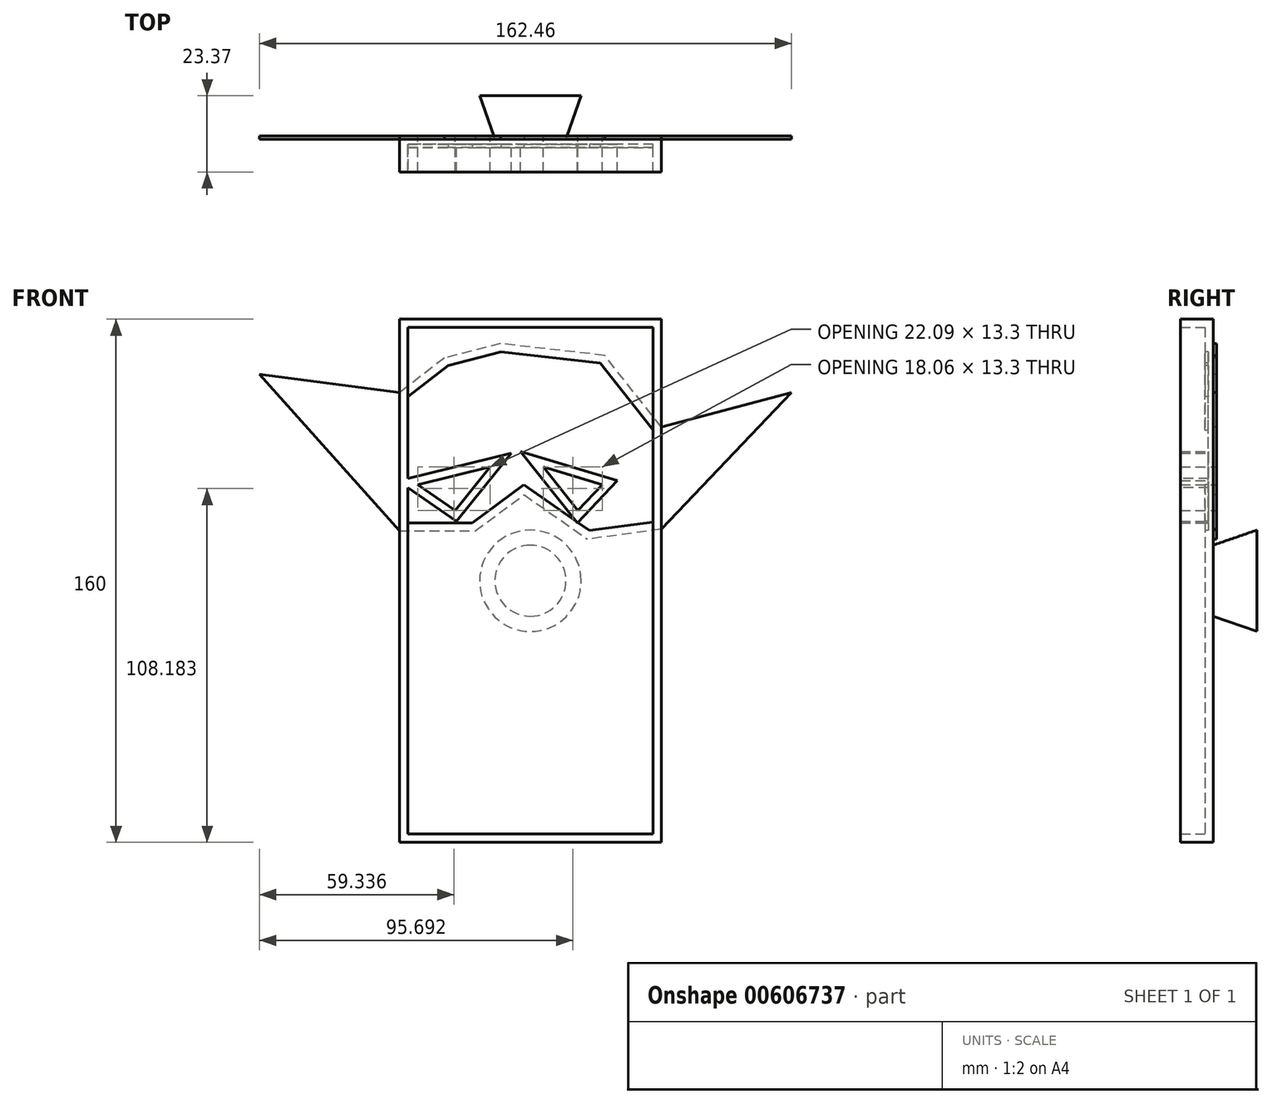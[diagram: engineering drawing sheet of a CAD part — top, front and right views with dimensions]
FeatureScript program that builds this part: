
annotation { "Feature Type Name" : "Feature", "Feature Type Description" : "" }
export const myFeature = defineFeature(function(context is Context, id is Id, definition is map)
    precondition{}
    {
        {
            var Q0;
            Q0=qCreatedBy(makeId("Front.planeOp"),FACE);
            var sketch = newSketch(context, id + "F0", { "sketchPlane" : qUnion([Q0])});
            skLineSegment(sketch, "E0.bottom", {"start": v(-40, 80) * mm, "end": v(40, 80) * mm});
            skLineSegment(sketch, "E0.top", {"start": v(-40, -80) * mm, "end": v(40, -80) * mm});
            skLineSegment(sketch, "E0.left", {"start": v(-40, 80) * mm, "end": v(-40, -80) * mm});
            skLineSegment(sketch, "E0.right", {"start": v(40, 80) * mm, "end": v(40, -80) * mm});
            skPoint(sketch, "E0.middle", {"position": v(0, 0) * mm});
            skSolve(sketch);
        }
        {
            var Q0;
            Q0=makeQuery(id+"F0.imprint","IMPRINT",FACE,{"disambiguationData":[TD([[makeQuery(id+"F0.imprint","IMPRINT",EDGE,{"derivedFrom":sQuery(id+"F0.wireOp",EDGE,"E0.bottom")}),-1.0]])]});
            extrude(context, id + "F1", {"entities" : qUnion([Q0]), "depth" : 10 * mm, "offsetDistance" : 25 * mm});
        }
        {
            var Q0;
            Q0=makeQuery(id+"F1.opExtrude","CAP_FACE",FACE,{"disambiguationData":[OSD([sQuery(id+"F0.wireOp",EDGE,"E0.bottom"),sQuery(id+"F0.wireOp",EDGE,"E0.top"),sQuery(id+"F0.wireOp",EDGE,"E0.left"),sQuery(id+"F0.wireOp",EDGE,"E0.right")])],"isStart":true});
            var sketch = newSketch(context, id + "F2", { "sketchPlane" : qUnion([Q0])});
            skLineSegment(sketch, "E1", {"start": v(-40, 15.78) * mm, "end": v(-79.71, 57.57) * mm});
            skLineSegment(sketch, "E2", {"start": v(-79.71, 57.57) * mm, "end": v(-40, 47.05) * mm});
            skLineSegment(sketch, "E3", {"start": v(-40, 47.05) * mm, "end": v(-22.7, 68.92) * mm});
            skLineSegment(sketch, "E4", {"start": v(-22.7, 68.92) * mm, "end": v(9.13, 72.51) * mm});
            skLineSegment(sketch, "E5", {"start": v(9.13, 72.51) * mm, "end": v(26.3, 68.09) * mm});
            skLineSegment(sketch, "E6", {"start": v(26.3, 68.09) * mm, "end": v(40, 57.57) * mm});
            skLineSegment(sketch, "E7", {"start": v(40, 57.57) * mm, "end": v(82.75, 63.1) * mm});
            skLineSegment(sketch, "E8", {"start": v(82.75, 63.1) * mm, "end": v(40, 15.22) * mm});
            skLineSegment(sketch, "E9", {"start": v(40, 15.22) * mm, "end": v(16.88, 15.22) * mm});
            skLineSegment(sketch, "E10", {"start": v(16.88, 15.22) * mm, "end": v(1.94, 26.3) * mm});
            skLineSegment(sketch, "E11", {"start": v(1.94, 26.3) * mm, "end": v(-17.44, 12.73) * mm});
            skLineSegment(sketch, "E12", {"start": v(-40, 15.78) * mm, "end": v(-17.44, 12.73) * mm});
            skSolve(sketch);
        }
        {
            var Q0;
            {var subQ0=sQuery(id+"F2.wireOp",EDGE,"E1");Q0=makeQuery(id+"F2.imprint","IMPRINT",FACE,{"disambiguationData":[TD([[makeQuery(id+"F2.imprint","IMPRINT",EDGE,{"derivedFrom":subQ0}),-1.0]])]});}
            var Q1;
            {var subQ0=sQuery(id+"F2.wireOp",EDGE,"E7");Q1=makeQuery(id+"F2.imprint","IMPRINT",FACE,{"disambiguationData":[TD([[makeQuery(id+"F2.imprint","IMPRINT",EDGE,{"derivedFrom":subQ0}),-1.0]])]});}
            var Q2;
            {var subQ3=sQuery(id+"F2.wireOp",EDGE,"E3");Q2=makeQuery(id+"F2.imprint","IMPRINT",FACE,{"disambiguationData":[TD([[makeQuery(id+"F2.imprint","IMPRINT",EDGE,{"derivedFrom":subQ3}),-1.0]])]});}
            extrude(context, id + "F3", {"entities" : qUnion([Q0, Q1, Q2]), "operationType" : NewBodyOperationType.ADD, "depth" : 1 * mm, "offsetDistance" : 25 * mm});
        }
        {
            var Q0;
            Q0=makeQuery(id+"F3.opExtrude","CAP_FACE",FACE,{"disambiguationData":[OSD([sQuery(id+"F2.wireOp",EDGE,"E1"),sQuery(id+"F2.wireOp",EDGE,"E2"),sQuery(id+"F2.wireOp",EDGE,"E3"),sQuery(id+"F2.wireOp",EDGE,"E4"),sQuery(id+"F2.wireOp",EDGE,"E5"),sQuery(id+"F2.wireOp",EDGE,"E6"),sQuery(id+"F2.wireOp",EDGE,"E7"),sQuery(id+"F2.wireOp",EDGE,"E8"),sQuery(id+"F2.wireOp",EDGE,"E9"),sQuery(id+"F2.wireOp",EDGE,"E10"),sQuery(id+"F2.wireOp",EDGE,"E11"),sQuery(id+"F2.wireOp",EDGE,"E12")])],"isStart":false});
            var sketch = newSketch(context, id + "F4", { "sketchPlane" : qUnion([Q0])});
            skLineSegment(sketch, "E13", {"start": v(-14.5, 21.53) * mm, "end": v(-21.97, 29.4) * mm});
            skLineSegment(sketch, "E14", {"start": v(-21.97, 29.4) * mm, "end": v(-3.91, 34.83) * mm});
            skLineSegment(sketch, "E15", {"start": v(-3.91, 34.83) * mm, "end": v(-14.5, 21.53) * mm});
            skLineSegment(sketch, "E16", {"start": v(23.04, 21.53) * mm, "end": v(12.37, 34.83) * mm});
            skLineSegment(sketch, "E17", {"start": v(12.37, 34.83) * mm, "end": v(34.46, 29.4) * mm});
            skLineSegment(sketch, "E18", {"start": v(34.46, 29.4) * mm, "end": v(23.04, 21.53) * mm});
            skSolve(sketch);
        }
        {
            var Q0;
            Q0 = qSketchRegion(id + "F4", true);
            extrude(context, id + "F5", {"entities" : qUnion([Q0]), "operationType" : NewBodyOperationType.REMOVE, "oppositeDirection" : true, "depth" : 25 * mm, "offsetDistance" : 25 * mm});
        }
        {
            var Q0;
            {var subQ2=sQuery(id+"F0.wireOp",EDGE,"E0.right");var subQ4=sQuery(id+"F0.wireOp",EDGE,"E0.left");var subQ6=sQuery(id+"F0.wireOp",EDGE,"E0.top");Q0=makeQuery(id+"F3.boolean.opBoolean","SPLIT",FACE,{"disambiguationData":[TD([makeQuery(id+"F1.opExtrude","SWEPT_FACE",FACE,{"disambiguationData":[OSD([subQ6])]})])],"derivedFrom":makeQuery(id+"F1.opExtrude","CAP_FACE",FACE,{"disambiguationData":[OSD([sQuery(id+"F0.wireOp",EDGE,"E0.bottom"),subQ6,subQ4,subQ2])],"isStart":true})});}
            var sketch = newSketch(context, id + "F6", { "sketchPlane" : qUnion([Q0])});
            skSolve(sketch);
        }
        {
            var Q0;
            Q0=makeQuery(id+"F1.opExtrude","CAP_FACE",FACE,{"disambiguationData":[OSD([sQuery(id+"F0.wireOp",EDGE,"E0.bottom"),sQuery(id+"F0.wireOp",EDGE,"E0.top"),sQuery(id+"F0.wireOp",EDGE,"E0.left"),sQuery(id+"F0.wireOp",EDGE,"E0.right")])],"isStart":false});
            shell(context, id + "F7", {"entities" : qUnion([Q0]), "thickness" : 2.5 * mm});
        }
        {
            var Q0;
            Q0=qCreatedBy(makeId("Top.planeOp"),FACE);
            var sketch = newSketch(context, id + "F8", { "sketchPlane" : qUnion([Q0])});
            skLineSegment(sketch, "E19", {"start": v(0, 0) * mm, "end": v(10.88, 0) * mm});
            skLineSegment(sketch, "E20", {"start": v(10.88, 0) * mm, "end": v(15.51, 13.37) * mm});
            skLineSegment(sketch, "E21", {"start": v(15.51, 13.37) * mm, "end": v(0, 13.37) * mm});
            skLineSegment(sketch, "E22", {"start": v(0, 13.37) * mm, "end": v(0, 0) * mm});
            skPoint(sketch, "E23.orphan", {"position": v(-10.95, 0) * mm});
            skSolve(sketch);
        }
        {
            var Q0;
            Q0=makeQuery(id+"F8.imprint","IMPRINT",FACE,{"disambiguationData":[TD([[makeQuery(id+"F8.imprint","IMPRINT",EDGE,{"derivedFrom":sQuery(id+"F8.wireOp",EDGE,"E19")}),1.0]])]});
            var Q1;
            Q1=sQuery(id+"F8.wireOp",EDGE,"E22");
            revolve(context, id + "F9", {"operationType" : NewBodyOperationType.ADD, "surfaceOperationType" : NewSurfaceOperationType.NEW, "entities" : qUnion([Q0]), "axis" : qUnion([Q1]), "revolveType" : RevolveType.FULL});
        }
    });
